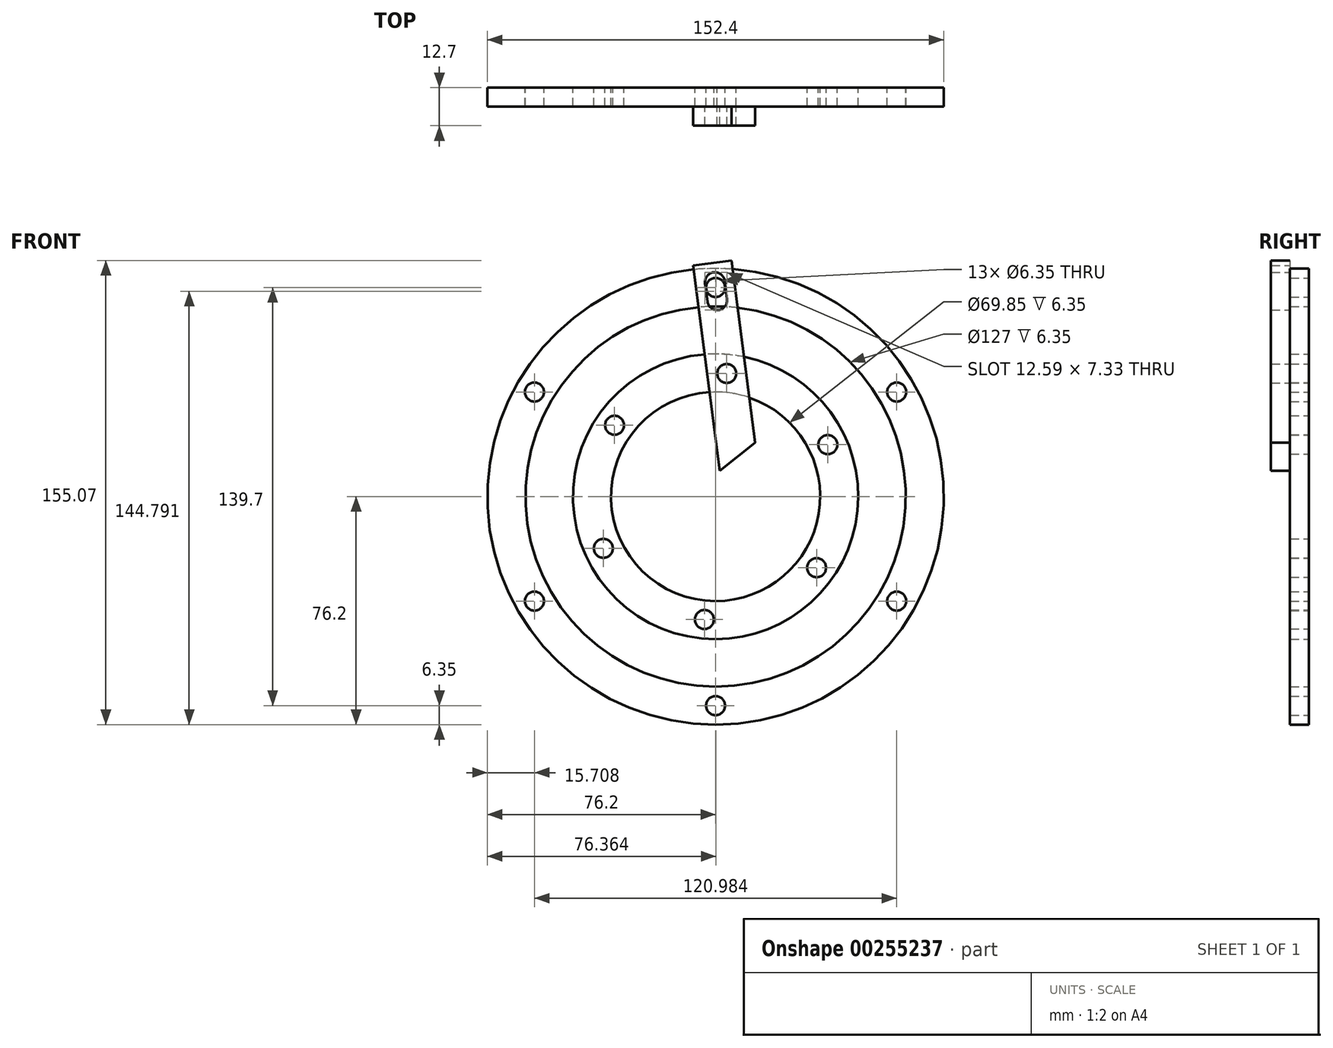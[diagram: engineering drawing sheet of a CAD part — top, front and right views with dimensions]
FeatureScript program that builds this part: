
annotation { "Feature Type Name" : "Feature", "Feature Type Description" : "" }
export const myFeature = defineFeature(function(context is Context, id is Id, definition is map)
    precondition{}
    {
        {
            var Q0;
            Q0=qCreatedBy(makeId("Front.planeOp"),FACE);
            var sketch = newSketch(context, id + "F0", { "sketchPlane" : qUnion([Q0])});
            skCircle(sketch, "E0", {"center": v(0, 0) * mm, "radius": 76.2 * mm});
            skCircle(sketch, "E1", {"center": v(0, 0) * mm, "radius": 63.5 * mm});
            skCircle(sketch, "E2", {"center": v(0, 69.85) * mm, "radius": 3.18 * mm});
            skCircle(sketch, "E3", {"center": v(60.5, 34.93) * mm, "radius": 3.18 * mm});
            skCircle(sketch, "E4", {"center": v(60.5, -34.92) * mm, "radius": 3.18 * mm});
            skCircle(sketch, "E5", {"center": v(0, -69.85) * mm, "radius": 3.18 * mm});
            skCircle(sketch, "E6", {"center": v(-60.5, 34.92) * mm, "radius": 3.18 * mm});
            skCircle(sketch, "E7", {"center": v(-60.5, -34.93) * mm, "radius": 3.18 * mm});
            skCircle(sketch, "E8", {"center": v(0, 0) * mm, "radius": 69.85 * mm, "construction": true});
            skLineSegment(sketch, "E9", {"start": v(0, 0) * mm, "end": v(0, 69.85) * mm, "construction": true});
            skLineSegment(sketch, "E10", {"start": v(0, 0) * mm, "end": v(60.5, 34.93) * mm, "construction": true});
            skLineSegment(sketch, "E11", {"start": v(0, 0) * mm, "end": v(60.5, -34.92) * mm, "construction": true});
            skLineSegment(sketch, "E12", {"start": v(0, 0) * mm, "end": v(0, -69.85) * mm, "construction": true});
            skLineSegment(sketch, "E13", {"start": v(0, 0) * mm, "end": v(-60.5, -34.93) * mm, "construction": true});
            skLineSegment(sketch, "E14", {"start": v(0, 0) * mm, "end": v(-60.5, 34.92) * mm, "construction": true});
            skSolve(sketch);
        }
        {
            var Q0;
            Q0 = qSketchRegion(id + "F0", true);
            extrude(context, id + "F1", {"entities" : qUnion([Q0]), "depth" : 6.35 * mm});
        }
        {
            var Q0;
            Q0=qCreatedBy(makeId("Front.planeOp"),FACE);
            var sketch = newSketch(context, id + "F2", { "sketchPlane" : qUnion([Q0])});
            skCircle(sketch, "E15", {"center": v(0, 0) * mm, "radius": 47.62 * mm});
            skCircle(sketch, "E16", {"center": v(0, 0) * mm, "radius": 34.93 * mm});
            skCircle(sketch, "E17", {"center": v(3.73, 41.1) * mm, "radius": 3.18 * mm});
            skCircle(sketch, "E18", {"center": v(37.47, 17.32) * mm, "radius": 3.18 * mm});
            skCircle(sketch, "E19", {"center": v(33.73, -23.79) * mm, "radius": 3.18 * mm});
            skCircle(sketch, "E20", {"center": v(-3.73, -41.1) * mm, "radius": 3.18 * mm});
            skCircle(sketch, "E21", {"center": v(-37.47, -17.32) * mm, "radius": 3.18 * mm});
            skCircle(sketch, "E22", {"center": v(-33.73, 23.79) * mm, "radius": 3.18 * mm});
            skCircle(sketch, "E23", {"center": v(0, 0) * mm, "radius": 41.28 * mm, "construction": true});
            skLineSegment(sketch, "E24", {"start": v(0, 0) * mm, "end": v(3.73, 41.1) * mm, "construction": true});
            skLineSegment(sketch, "E25", {"start": v(37.47, 17.32) * mm, "end": v(0, 0) * mm, "construction": true});
            skLineSegment(sketch, "E26", {"start": v(33.73, -23.79) * mm, "end": v(0, 0) * mm, "construction": true});
            skLineSegment(sketch, "E27", {"start": v(-3.73, -41.1) * mm, "end": v(0, 0) * mm, "construction": true});
            skLineSegment(sketch, "E28", {"start": v(-37.47, -17.32) * mm, "end": v(0, 0) * mm, "construction": true});
            skLineSegment(sketch, "E29", {"start": v(-33.73, 23.79) * mm, "end": v(0, 0) * mm, "construction": true});
            skSolve(sketch);
        }
        {
            var Q0;
            Q0 = qSketchRegion(id + "F2", true);
            extrude(context, id + "F3", {"entities" : qUnion([Q0]), "depth" : 6.35 * mm});
        }
        {
            var Q0;
            Q0=makeQuery(id+"F3.opExtrude","CAP_FACE",FACE,{"disambiguationData":[OSD([sQuery(id+"F2.wireOp",EDGE,"E15"),sQuery(id+"F2.wireOp",EDGE,"E16"),sQuery(id+"F2.wireOp",EDGE,"E17"),sQuery(id+"F2.wireOp",EDGE,"E18"),sQuery(id+"F2.wireOp",EDGE,"E19"),sQuery(id+"F2.wireOp",EDGE,"E20"),sQuery(id+"F2.wireOp",EDGE,"E21"),sQuery(id+"F2.wireOp",EDGE,"E22")])],"isStart":false});
            var sketch = newSketch(context, id + "F4", { "sketchPlane" : qUnion([Q0])});
            skCircle(sketch, "E30", {"center": v(3.73, 41.1) * mm, "radius": 3.18 * mm});
            skLineSegment(sketch, "E31", {"start": v(-7.49, 77.2) * mm, "end": v(1.42, 8.6) * mm});
            skLineSegment(sketch, "E32", {"start": v(1.42, 8.6) * mm, "end": v(13.26, 18.02) * mm});
            skLineSegment(sketch, "E33", {"start": v(13.26, 18.02) * mm, "end": v(5.36, 78.87) * mm});
            skLineSegment(sketch, "E34", {"start": v(5.36, 78.87) * mm, "end": v(-7.49, 77.2) * mm});
            skArc(sketch, "E35", {"start": v(3.05, 72.04) * mm, "mid": v(-0.65, 74.89) * mm, "end": v(-3.5, 71.19) * mm});
            skArc(sketch, "E36", {"start": v(-2.72, 65.14) * mm, "mid": v(0.98, 62.3) * mm, "end": v(3.83, 66) * mm});
            skLineSegment(sketch, "E37", {"start": v(3.05, 72.04) * mm, "end": v(3.83, 66) * mm});
            skLineSegment(sketch, "E38", {"start": v(-3.5, 71.19) * mm, "end": v(-2.72, 65.14) * mm});
            skLineSegment(sketch, "E39", {"start": v(3.73, 41.1) * mm, "end": v(-0.23, 71.61) * mm, "construction": true});
            skPoint(sketch, "E40", {"position": v(0, 69.85) * mm});
            skSolve(sketch);
        }
        {
            var Q0;
            Q0 = qSketchRegion(id + "F4", true);
            extrude(context, id + "F5", {"entities" : qUnion([Q0]), "depth" : 6.35 * mm});
        }
    });
